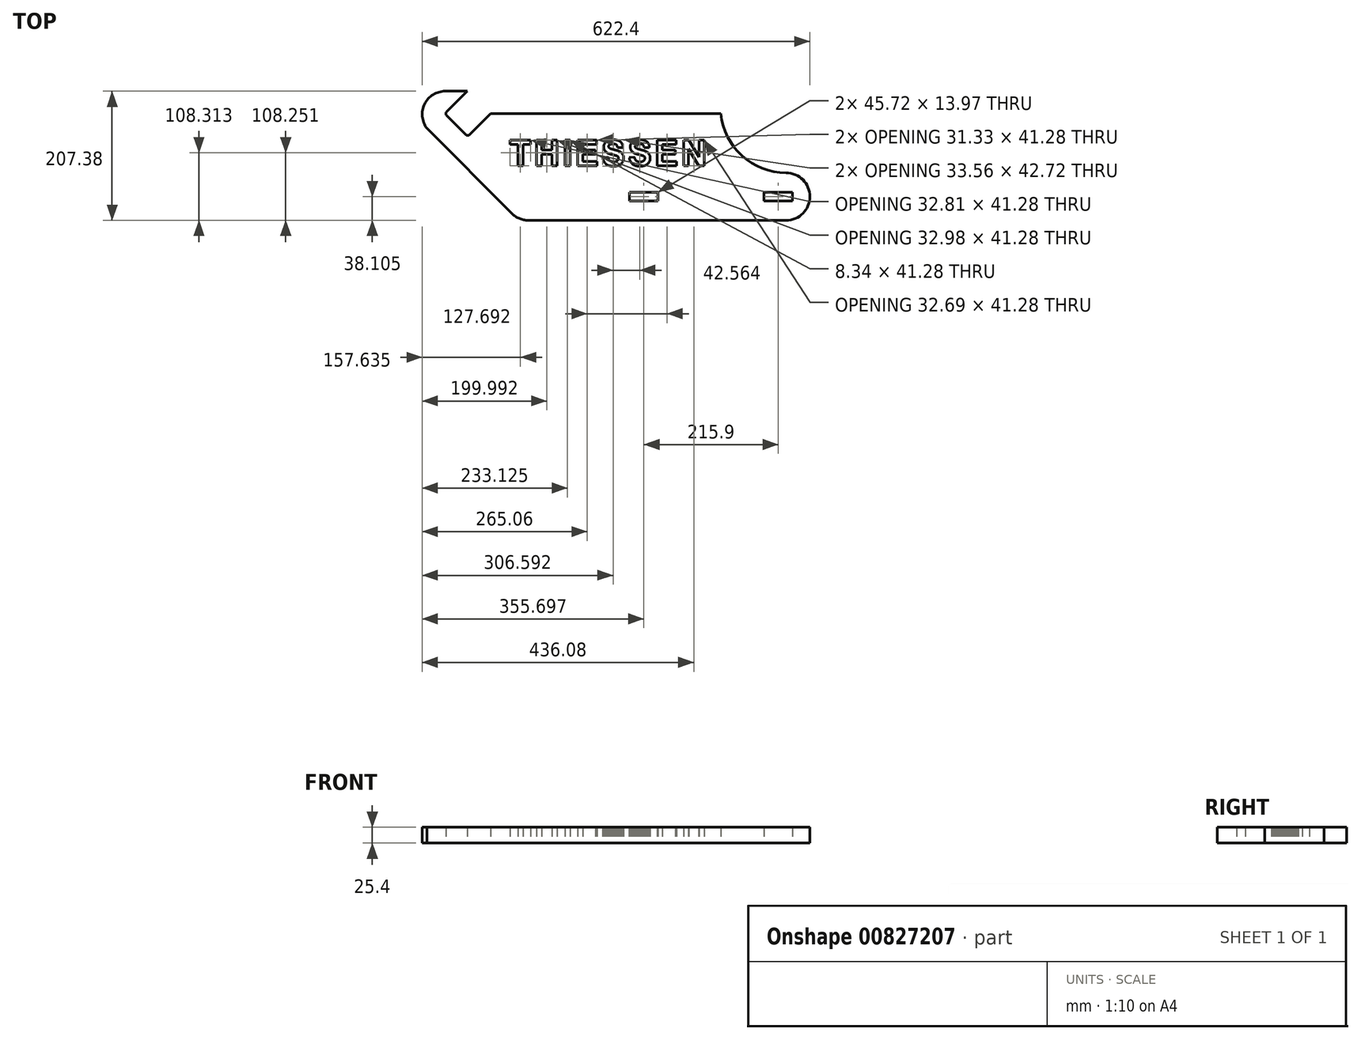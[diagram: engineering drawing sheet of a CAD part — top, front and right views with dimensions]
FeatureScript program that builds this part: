
annotation { "Feature Type Name" : "Feature", "Feature Type Description" : "" }
export const myFeature = defineFeature(function(context is Context, id is Id, definition is map)
    precondition{}
    {
        {
            var Q0;
            Q0=qCreatedBy(makeId("Top.planeOp"),FACE);
            var sketch = newSketch(context, id + "F0", { "sketchPlane" : qUnion([Q0])});
            skLineSegment(sketch, "E0", {"start": v(-238.98, 103.69) * mm, "end": v(-274, 103.69) * mm});
            skArc(sketch, "E1", {"start": v(-274, 103.69) * mm, "mid": v(-307.3, 83.06) * mm, "end": v(-303.67, 44.05) * mm});
            skArc(sketch, "E2", {"start": v(-167.33, -92.8) * mm, "mid": v(-155.26, -100.85) * mm, "end": v(-141.02, -103.69) * mm});
            skLineSegment(sketch, "E3", {"start": v(-141.02, -103.69) * mm, "end": v(273.1, -103.69) * mm});
            skArc(sketch, "E4", {"start": v(273.1, -103.69) * mm, "mid": v(311.2, -65.59) * mm, "end": v(273.1, -27.49) * mm});
            skArc(sketch, "E5", {"start": v(168.32, 67.76) * mm, "mid": v(202.3, -0.11) * mm, "end": v(273.1, -27.49) * mm});
            skLineSegment(sketch, "E6", {"start": v(-201.26, 67.76) * mm, "end": v(168.32, 67.76) * mm});
            skLineSegment(sketch, "E7", {"start": v(-303.67, 44.05) * mm, "end": v(-167.33, -92.8) * mm});
            skLineSegment(sketch, "E8", {"start": v(-272.2, 70.46) * mm, "end": v(-238.98, 103.69) * mm});
            skLineSegment(sketch, "E9", {"start": v(-240.77, 33.64) * mm, "end": v(-272.2, 65.07) * mm});
            skLineSegment(sketch, "E10", {"start": v(-201.26, 67.76) * mm, "end": v(-235.38, 33.64) * mm});
            skLineSegment(sketch, "E11", {"start": v(67.36, -58.6) * mm, "end": v(21.64, -58.6) * mm});
            skLineSegment(sketch, "E12", {"start": v(21.64, -72.57) * mm, "end": v(21.64, -58.6) * mm});
            skLineSegment(sketch, "E13", {"start": v(67.36, -72.57) * mm, "end": v(21.64, -72.57) * mm});
            skLineSegment(sketch, "E14", {"start": v(67.36, -72.57) * mm, "end": v(67.36, -58.6) * mm});
            skLineSegment(sketch, "E15", {"start": v(283.26, -58.6) * mm, "end": v(237.54, -58.6) * mm});
            skLineSegment(sketch, "E16", {"start": v(283.26, -72.57) * mm, "end": v(283.26, -58.6) * mm});
            skLineSegment(sketch, "E17", {"start": v(283.26, -72.57) * mm, "end": v(237.54, -72.57) * mm});
            skLineSegment(sketch, "E18", {"start": v(237.54, -72.57) * mm, "end": v(237.54, -58.6) * mm});
            skArc(sketch, "E19", {"start": v(-240.77, 33.64) * mm, "mid": v(-238.08, 32.52) * mm, "end": v(-235.38, 33.64) * mm});
            skArc(sketch, "E20", {"start": v(-272.2, 70.46) * mm, "mid": v(-273.32, 67.76) * mm, "end": v(-272.2, 65.07) * mm});
            skLineSegment(sketch, "E21", {"start": v(-157.71, -16.01) * mm, "end": v(-157.71, 18.28) * mm});
            skLineSegment(sketch, "E22", {"start": v(-157.71, 18.28) * mm, "end": v(-169.97, 18.28) * mm});
            skLineSegment(sketch, "E23", {"start": v(-169.97, 18.28) * mm, "end": v(-169.97, 25.26) * mm});
            skLineSegment(sketch, "E24", {"start": v(-169.97, 25.26) * mm, "end": v(-137.16, 25.26) * mm});
            skLineSegment(sketch, "E25", {"start": v(-137.16, 25.26) * mm, "end": v(-137.16, 18.28) * mm});
            skLineSegment(sketch, "E26", {"start": v(-137.16, 18.28) * mm, "end": v(-149.38, 18.28) * mm});
            skLineSegment(sketch, "E27", {"start": v(-149.38, 18.28) * mm, "end": v(-149.38, -16.01) * mm});
            skLineSegment(sketch, "E28", {"start": v(-149.38, -16.01) * mm, "end": v(-157.71, -16.01) * mm});
            skLineSegment(sketch, "E29", {"start": v(-127.7, -16.01) * mm, "end": v(-127.7, 25.26) * mm});
            skLineSegment(sketch, "E30", {"start": v(-127.7, 25.26) * mm, "end": v(-119.36, 25.26) * mm});
            skLineSegment(sketch, "E31", {"start": v(-119.36, 25.26) * mm, "end": v(-119.36, 9) * mm});
            skLineSegment(sketch, "E32", {"start": v(-119.36, 9) * mm, "end": v(-103.06, 9) * mm});
            skLineSegment(sketch, "E33", {"start": v(-103.06, 9) * mm, "end": v(-103.06, 25.26) * mm});
            skLineSegment(sketch, "E34", {"start": v(-103.06, 25.26) * mm, "end": v(-94.72, 25.26) * mm});
            skLineSegment(sketch, "E35", {"start": v(-94.72, 25.26) * mm, "end": v(-94.72, -16.01) * mm});
            skLineSegment(sketch, "E36", {"start": v(-94.72, -16.01) * mm, "end": v(-103.06, -16.01) * mm});
            skLineSegment(sketch, "E37", {"start": v(-103.06, -16.01) * mm, "end": v(-103.06, 2.02) * mm});
            skLineSegment(sketch, "E38", {"start": v(-103.06, 2.02) * mm, "end": v(-119.36, 2.02) * mm});
            skLineSegment(sketch, "E39", {"start": v(-119.36, 2.02) * mm, "end": v(-119.36, -16.01) * mm});
            skLineSegment(sketch, "E40", {"start": v(-119.36, -16.01) * mm, "end": v(-127.7, -16.01) * mm});
            skLineSegment(sketch, "E41", {"start": v(-82.24, -16.01) * mm, "end": v(-82.24, 25.26) * mm});
            skLineSegment(sketch, "E42", {"start": v(-82.24, 25.26) * mm, "end": v(-73.9, 25.26) * mm});
            skLineSegment(sketch, "E43", {"start": v(-73.9, 25.26) * mm, "end": v(-73.9, -16.01) * mm});
            skLineSegment(sketch, "E44", {"start": v(-73.9, -16.01) * mm, "end": v(-82.24, -16.01) * mm});
            skLineSegment(sketch, "E45", {"start": v(-61.8, -16.01) * mm, "end": v(-61.8, 25.26) * mm});
            skLineSegment(sketch, "E46", {"start": v(-61.8, 25.26) * mm, "end": v(-31.26, 25.26) * mm});
            skLineSegment(sketch, "E47", {"start": v(-31.26, 25.26) * mm, "end": v(-31.26, 18.28) * mm});
            skLineSegment(sketch, "E48", {"start": v(-31.26, 18.28) * mm, "end": v(-53.47, 18.28) * mm});
            skLineSegment(sketch, "E49", {"start": v(-53.47, 18.28) * mm, "end": v(-53.47, 9.12) * mm});
            skLineSegment(sketch, "E50", {"start": v(-53.47, 9.12) * mm, "end": v(-32.79, 9.12) * mm});
            skLineSegment(sketch, "E51", {"start": v(-32.79, 9.12) * mm, "end": v(-32.79, 2.15) * mm});
            skLineSegment(sketch, "E52", {"start": v(-32.79, 2.15) * mm, "end": v(-53.47, 2.15) * mm});
            skLineSegment(sketch, "E53", {"start": v(-53.47, 2.15) * mm, "end": v(-53.47, -9.04) * mm});
            skLineSegment(sketch, "E54", {"start": v(-53.47, -9.04) * mm, "end": v(-30.48, -9.04) * mm});
            skLineSegment(sketch, "E55", {"start": v(-30.48, -9.04) * mm, "end": v(-30.48, -16.01) * mm});
            skLineSegment(sketch, "E56", {"start": v(-30.48, -16.01) * mm, "end": v(-61.8, -16.01) * mm});
            skLineSegment(sketch, "E57", {"start": v(-21.39, -2.64) * mm, "end": v(-13.3, -1.86) * mm});
            skLineSegment(sketch, "E58", {"start": v(-13.3, -1.86) * mm, "end": v(-13.09, -2.85) * mm});
            skLineSegment(sketch, "E59", {"start": v(-13.09, -2.85) * mm, "end": v(-12.84, -3.77) * mm});
            skLineSegment(sketch, "E60", {"start": v(-12.84, -3.77) * mm, "end": v(-12.53, -4.62) * mm});
            skLineSegment(sketch, "E61", {"start": v(-12.53, -4.62) * mm, "end": v(-12.19, -5.4) * mm});
            skLineSegment(sketch, "E62", {"start": v(-12.19, -5.4) * mm, "end": v(-11.8, -6.12) * mm});
            skLineSegment(sketch, "E63", {"start": v(-11.8, -6.12) * mm, "end": v(-11.35, -6.77) * mm});
            skLineSegment(sketch, "E64", {"start": v(-11.35, -6.77) * mm, "end": v(-10.86, -7.35) * mm});
            skLineSegment(sketch, "E65", {"start": v(-10.86, -7.35) * mm, "end": v(-10.32, -7.86) * mm});
            skLineSegment(sketch, "E66", {"start": v(-10.32, -7.86) * mm, "end": v(-9.74, -8.31) * mm});
            skLineSegment(sketch, "E67", {"start": v(-9.74, -8.31) * mm, "end": v(-9.1, -8.7) * mm});
            skLineSegment(sketch, "E68", {"start": v(-9.1, -8.7) * mm, "end": v(-8.42, -9.03) * mm});
            skLineSegment(sketch, "E69", {"start": v(-8.42, -9.03) * mm, "end": v(-7.7, -9.3) * mm});
            skLineSegment(sketch, "E70", {"start": v(-7.7, -9.3) * mm, "end": v(-6.91, -9.51) * mm});
            skLineSegment(sketch, "E71", {"start": v(-6.91, -9.51) * mm, "end": v(-6.08, -9.66) * mm});
            skLineSegment(sketch, "E72", {"start": v(-6.08, -9.66) * mm, "end": v(-5.2, -9.75) * mm});
            skLineSegment(sketch, "E73", {"start": v(-5.2, -9.75) * mm, "end": v(-4.28, -9.78) * mm});
            skLineSegment(sketch, "E74", {"start": v(-4.28, -9.78) * mm, "end": v(-3.3, -9.76) * mm});
            skLineSegment(sketch, "E75", {"start": v(-3.3, -9.76) * mm, "end": v(-2.4, -9.68) * mm});
            skLineSegment(sketch, "E76", {"start": v(-2.4, -9.68) * mm, "end": v(-1.54, -9.54) * mm});
            skLineSegment(sketch, "E77", {"start": v(-1.54, -9.54) * mm, "end": v(-0.75, -9.36) * mm});
            skLineSegment(sketch, "E78", {"start": v(-0.75, -9.36) * mm, "end": v(-0.02, -9.12) * mm});
            skLineSegment(sketch, "E79", {"start": v(-0.02, -9.12) * mm, "end": v(0.65, -8.82) * mm});
            skLineSegment(sketch, "E80", {"start": v(0.65, -8.82) * mm, "end": v(1.25, -8.48) * mm});
            skLineSegment(sketch, "E81", {"start": v(1.25, -8.48) * mm, "end": v(1.8, -8.08) * mm});
            skLineSegment(sketch, "E82", {"start": v(1.8, -8.08) * mm, "end": v(2.41, -7.5) * mm});
            skLineSegment(sketch, "E83", {"start": v(2.41, -7.5) * mm, "end": v(2.93, -6.88) * mm});
            skLineSegment(sketch, "E84", {"start": v(2.93, -6.88) * mm, "end": v(3.32, -6.23) * mm});
            skLineSegment(sketch, "E85", {"start": v(3.32, -6.23) * mm, "end": v(3.6, -5.55) * mm});
            skLineSegment(sketch, "E86", {"start": v(3.6, -5.55) * mm, "end": v(3.78, -4.83) * mm});
            skLineSegment(sketch, "E87", {"start": v(3.78, -4.83) * mm, "end": v(3.83, -4.09) * mm});
            skLineSegment(sketch, "E88", {"start": v(3.83, -4.09) * mm, "end": v(3.74, -3.16) * mm});
            skLineSegment(sketch, "E89", {"start": v(3.74, -3.16) * mm, "end": v(3.45, -2.33) * mm});
            skLineSegment(sketch, "E90", {"start": v(3.45, -2.33) * mm, "end": v(2.97, -1.6) * mm});
            skLineSegment(sketch, "E91", {"start": v(2.97, -1.6) * mm, "end": v(2.47, -1.1) * mm});
            skLineSegment(sketch, "E92", {"start": v(2.47, -1.1) * mm, "end": v(1.8, -0.63) * mm});
            skLineSegment(sketch, "E93", {"start": v(1.8, -0.63) * mm, "end": v(0.97, -0.2) * mm});
            skLineSegment(sketch, "E94", {"start": v(0.97, -0.2) * mm, "end": v(-0.02, 0.2) * mm});
            skLineSegment(sketch, "E95", {"start": v(-0.02, 0.2) * mm, "end": v(-0.45, 0.34) * mm});
            skLineSegment(sketch, "E96", {"start": v(-0.45, 0.34) * mm, "end": v(-1, 0.5) * mm});
            skLineSegment(sketch, "E97", {"start": v(-1, 0.5) * mm, "end": v(-1.65, 0.69) * mm});
            skLineSegment(sketch, "E98", {"start": v(-1.65, 0.69) * mm, "end": v(-2.42, 0.9) * mm});
            skLineSegment(sketch, "E99", {"start": v(-2.42, 0.9) * mm, "end": v(-3.32, 1.14) * mm});
            skLineSegment(sketch, "E100", {"start": v(-3.32, 1.14) * mm, "end": v(-4.33, 1.4) * mm});
            skLineSegment(sketch, "E101", {"start": v(-4.33, 1.4) * mm, "end": v(-5.45, 1.69) * mm});
            skLineSegment(sketch, "E102", {"start": v(-5.45, 1.69) * mm, "end": v(-6.7, 2) * mm});
            skLineSegment(sketch, "E103", {"start": v(-6.7, 2) * mm, "end": v(-7.78, 2.28) * mm});
            skLineSegment(sketch, "E104", {"start": v(-7.78, 2.28) * mm, "end": v(-8.82, 2.58) * mm});
            skLineSegment(sketch, "E105", {"start": v(-8.82, 2.58) * mm, "end": v(-9.8, 2.88) * mm});
            skLineSegment(sketch, "E106", {"start": v(-9.8, 2.88) * mm, "end": v(-10.72, 3.2) * mm});
            skLineSegment(sketch, "E107", {"start": v(-10.72, 3.2) * mm, "end": v(-11.59, 3.52) * mm});
            skLineSegment(sketch, "E108", {"start": v(-11.59, 3.52) * mm, "end": v(-12.4, 3.85) * mm});
            skLineSegment(sketch, "E109", {"start": v(-12.4, 3.85) * mm, "end": v(-13.15, 4.2) * mm});
            skLineSegment(sketch, "E110", {"start": v(-13.15, 4.2) * mm, "end": v(-13.85, 4.56) * mm});
            skLineSegment(sketch, "E111", {"start": v(-13.85, 4.56) * mm, "end": v(-14.5, 4.92) * mm});
            skLineSegment(sketch, "E112", {"start": v(-14.5, 4.92) * mm, "end": v(-15.09, 5.3) * mm});
            skLineSegment(sketch, "E113", {"start": v(-15.09, 5.3) * mm, "end": v(-15.62, 5.69) * mm});
            skLineSegment(sketch, "E114", {"start": v(-15.62, 5.69) * mm, "end": v(-16.1, 6.09) * mm});
            skLineSegment(sketch, "E115", {"start": v(-16.1, 6.09) * mm, "end": v(-16.76, 6.72) * mm});
            skLineSegment(sketch, "E116", {"start": v(-16.76, 6.72) * mm, "end": v(-17.36, 7.38) * mm});
            skLineSegment(sketch, "E117", {"start": v(-17.36, 7.38) * mm, "end": v(-17.89, 8.06) * mm});
            skLineSegment(sketch, "E118", {"start": v(-17.89, 8.06) * mm, "end": v(-18.36, 8.76) * mm});
            skLineSegment(sketch, "E119", {"start": v(-18.36, 8.76) * mm, "end": v(-18.77, 9.5) * mm});
            skLineSegment(sketch, "E120", {"start": v(-18.77, 9.5) * mm, "end": v(-19.11, 10.25) * mm});
            skLineSegment(sketch, "E121", {"start": v(-19.11, 10.25) * mm, "end": v(-19.4, 11.03) * mm});
            skLineSegment(sketch, "E122", {"start": v(-19.4, 11.03) * mm, "end": v(-19.62, 11.83) * mm});
            skLineSegment(sketch, "E123", {"start": v(-19.62, 11.83) * mm, "end": v(-19.77, 12.66) * mm});
            skLineSegment(sketch, "E124", {"start": v(-19.77, 12.66) * mm, "end": v(-19.87, 13.52) * mm});
            skLineSegment(sketch, "E125", {"start": v(-19.87, 13.52) * mm, "end": v(-19.9, 14.4) * mm});
            skLineSegment(sketch, "E126", {"start": v(-19.9, 14.4) * mm, "end": v(-19.86, 15.3) * mm});
            skLineSegment(sketch, "E127", {"start": v(-19.86, 15.3) * mm, "end": v(-19.75, 16.17) * mm});
            skLineSegment(sketch, "E128", {"start": v(-19.75, 16.17) * mm, "end": v(-19.57, 17.03) * mm});
            skLineSegment(sketch, "E129", {"start": v(-19.57, 17.03) * mm, "end": v(-19.32, 17.87) * mm});
            skLineSegment(sketch, "E130", {"start": v(-19.32, 17.87) * mm, "end": v(-18.99, 18.7) * mm});
            skLineSegment(sketch, "E131", {"start": v(-18.99, 18.7) * mm, "end": v(-18.59, 19.5) * mm});
            skLineSegment(sketch, "E132", {"start": v(-18.59, 19.5) * mm, "end": v(-18.11, 20.3) * mm});
            skLineSegment(sketch, "E133", {"start": v(-18.11, 20.3) * mm, "end": v(-17.64, 20.97) * mm});
            skLineSegment(sketch, "E134", {"start": v(-17.64, 20.97) * mm, "end": v(-17.12, 21.6) * mm});
            skLineSegment(sketch, "E135", {"start": v(-17.12, 21.6) * mm, "end": v(-16.55, 22.18) * mm});
            skLineSegment(sketch, "E136", {"start": v(-16.55, 22.18) * mm, "end": v(-15.93, 22.72) * mm});
            skLineSegment(sketch, "E137", {"start": v(-15.93, 22.72) * mm, "end": v(-15.26, 23.22) * mm});
            skLineSegment(sketch, "E138", {"start": v(-15.26, 23.22) * mm, "end": v(-14.55, 23.68) * mm});
            skLineSegment(sketch, "E139", {"start": v(-14.55, 23.68) * mm, "end": v(-13.78, 24.1) * mm});
            skLineSegment(sketch, "E140", {"start": v(-13.78, 24.1) * mm, "end": v(-12.96, 24.48) * mm});
            skLineSegment(sketch, "E141", {"start": v(-12.96, 24.48) * mm, "end": v(-12.2, 24.79) * mm});
            skLineSegment(sketch, "E142", {"start": v(-12.2, 24.79) * mm, "end": v(-11.4, 25.05) * mm});
            skLineSegment(sketch, "E143", {"start": v(-11.4, 25.05) * mm, "end": v(-10.57, 25.28) * mm});
            skLineSegment(sketch, "E144", {"start": v(-10.57, 25.28) * mm, "end": v(-9.7, 25.48) * mm});
            skLineSegment(sketch, "E145", {"start": v(-9.7, 25.48) * mm, "end": v(-8.8, 25.64) * mm});
            skLineSegment(sketch, "E146", {"start": v(-8.8, 25.64) * mm, "end": v(-7.86, 25.76) * mm});
            skLineSegment(sketch, "E147", {"start": v(-7.86, 25.76) * mm, "end": v(-6.89, 25.85) * mm});
            skLineSegment(sketch, "E148", {"start": v(-6.89, 25.85) * mm, "end": v(-5.88, 25.9) * mm});
            skLineSegment(sketch, "E149", {"start": v(-5.88, 25.9) * mm, "end": v(-4.84, 25.92) * mm});
            skLineSegment(sketch, "E150", {"start": v(-4.84, 25.92) * mm, "end": v(-3.75, 25.9) * mm});
            skLineSegment(sketch, "E151", {"start": v(-3.75, 25.9) * mm, "end": v(-2.7, 25.85) * mm});
            skLineSegment(sketch, "E152", {"start": v(-2.7, 25.85) * mm, "end": v(-1.7, 25.76) * mm});
            skLineSegment(sketch, "E153", {"start": v(-1.7, 25.76) * mm, "end": v(-0.72, 25.64) * mm});
            skLineSegment(sketch, "E154", {"start": v(-0.72, 25.64) * mm, "end": v(0.22, 25.49) * mm});
            skLineSegment(sketch, "E155", {"start": v(0.22, 25.49) * mm, "end": v(1.1, 25.3) * mm});
            skLineSegment(sketch, "E156", {"start": v(1.1, 25.3) * mm, "end": v(1.96, 25.07) * mm});
            skLineSegment(sketch, "E157", {"start": v(1.96, 25.07) * mm, "end": v(2.78, 24.8) * mm});
            skLineSegment(sketch, "E158", {"start": v(2.78, 24.8) * mm, "end": v(3.56, 24.51) * mm});
            skLineSegment(sketch, "E159", {"start": v(3.56, 24.51) * mm, "end": v(4.3, 24.18) * mm});
            skLineSegment(sketch, "E160", {"start": v(4.3, 24.18) * mm, "end": v(5, 23.82) * mm});
            skLineSegment(sketch, "E161", {"start": v(5, 23.82) * mm, "end": v(5.65, 23.42) * mm});
            skLineSegment(sketch, "E162", {"start": v(5.65, 23.42) * mm, "end": v(6.27, 22.98) * mm});
            skLineSegment(sketch, "E163", {"start": v(6.27, 22.98) * mm, "end": v(6.85, 22.51) * mm});
            skLineSegment(sketch, "E164", {"start": v(6.85, 22.51) * mm, "end": v(7.48, 21.93) * mm});
            skLineSegment(sketch, "E165", {"start": v(7.48, 21.93) * mm, "end": v(8.06, 21.31) * mm});
            skLineSegment(sketch, "E166", {"start": v(8.06, 21.31) * mm, "end": v(8.58, 20.67) * mm});
            skLineSegment(sketch, "E167", {"start": v(8.58, 20.67) * mm, "end": v(9.05, 19.99) * mm});
            skLineSegment(sketch, "E168", {"start": v(9.05, 19.99) * mm, "end": v(9.48, 19.28) * mm});
            skLineSegment(sketch, "E169", {"start": v(9.48, 19.28) * mm, "end": v(9.84, 18.53) * mm});
            skLineSegment(sketch, "E170", {"start": v(9.84, 18.53) * mm, "end": v(10.16, 17.76) * mm});
            skLineSegment(sketch, "E171", {"start": v(10.16, 17.76) * mm, "end": v(10.43, 16.95) * mm});
            skLineSegment(sketch, "E172", {"start": v(10.43, 16.95) * mm, "end": v(10.64, 16.12) * mm});
            skLineSegment(sketch, "E173", {"start": v(10.64, 16.12) * mm, "end": v(10.8, 15.25) * mm});
            skLineSegment(sketch, "E174", {"start": v(10.8, 15.25) * mm, "end": v(10.92, 14.35) * mm});
            skLineSegment(sketch, "E175", {"start": v(10.92, 14.35) * mm, "end": v(10.97, 13.41) * mm});
            skLineSegment(sketch, "E176", {"start": v(10.97, 13.41) * mm, "end": v(2.64, 13.04) * mm});
            skLineSegment(sketch, "E177", {"start": v(2.64, 13.04) * mm, "end": v(2.42, 14.06) * mm});
            skLineSegment(sketch, "E178", {"start": v(2.42, 14.06) * mm, "end": v(2.14, 14.97) * mm});
            skLineSegment(sketch, "E179", {"start": v(2.14, 14.97) * mm, "end": v(1.8, 15.78) * mm});
            skLineSegment(sketch, "E180", {"start": v(1.8, 15.78) * mm, "end": v(1.38, 16.5) * mm});
            skLineSegment(sketch, "E181", {"start": v(1.38, 16.5) * mm, "end": v(0.9, 17.11) * mm});
            skLineSegment(sketch, "E182", {"start": v(0.9, 17.11) * mm, "end": v(0.34, 17.63) * mm});
            skLineSegment(sketch, "E183", {"start": v(0.34, 17.63) * mm, "end": v(-0.2, 18) * mm});
            skLineSegment(sketch, "E184", {"start": v(-0.2, 18) * mm, "end": v(-0.8, 18.31) * mm});
            skLineSegment(sketch, "E185", {"start": v(-0.8, 18.31) * mm, "end": v(-1.49, 18.57) * mm});
            skLineSegment(sketch, "E186", {"start": v(-1.49, 18.57) * mm, "end": v(-2.24, 18.77) * mm});
            skLineSegment(sketch, "E187", {"start": v(-2.24, 18.77) * mm, "end": v(-3.06, 18.91) * mm});
            skLineSegment(sketch, "E188", {"start": v(-3.06, 18.91) * mm, "end": v(-3.96, 19) * mm});
            skLineSegment(sketch, "E189", {"start": v(-3.96, 19) * mm, "end": v(-4.93, 19.03) * mm});
            skLineSegment(sketch, "E190", {"start": v(-4.93, 19.03) * mm, "end": v(-5.93, 19) * mm});
            skLineSegment(sketch, "E191", {"start": v(-5.93, 19) * mm, "end": v(-6.87, 18.9) * mm});
            skLineSegment(sketch, "E192", {"start": v(-6.87, 18.9) * mm, "end": v(-7.75, 18.75) * mm});
            skLineSegment(sketch, "E193", {"start": v(-7.75, 18.75) * mm, "end": v(-8.56, 18.54) * mm});
            skLineSegment(sketch, "E194", {"start": v(-8.56, 18.54) * mm, "end": v(-9.3, 18.26) * mm});
            skLineSegment(sketch, "E195", {"start": v(-9.3, 18.26) * mm, "end": v(-10, 17.93) * mm});
            skLineSegment(sketch, "E196", {"start": v(-10, 17.93) * mm, "end": v(-10.61, 17.53) * mm});
            skLineSegment(sketch, "E197", {"start": v(-10.61, 17.53) * mm, "end": v(-11.2, 17.01) * mm});
            skLineSegment(sketch, "E198", {"start": v(-11.2, 17.01) * mm, "end": v(-11.6, 16.41) * mm});
            skLineSegment(sketch, "E199", {"start": v(-11.6, 16.41) * mm, "end": v(-11.85, 15.73) * mm});
            skLineSegment(sketch, "E200", {"start": v(-11.85, 15.73) * mm, "end": v(-11.93, 14.96) * mm});
            skLineSegment(sketch, "E201", {"start": v(-11.93, 14.96) * mm, "end": v(-11.86, 14.26) * mm});
            skLineSegment(sketch, "E202", {"start": v(-11.86, 14.26) * mm, "end": v(-11.62, 13.6) * mm});
            skLineSegment(sketch, "E203", {"start": v(-11.62, 13.6) * mm, "end": v(-11.24, 13) * mm});
            skLineSegment(sketch, "E204", {"start": v(-11.24, 13) * mm, "end": v(-10.7, 12.45) * mm});
            skLineSegment(sketch, "E205", {"start": v(-10.7, 12.45) * mm, "end": v(-10.33, 12.19) * mm});
            skLineSegment(sketch, "E206", {"start": v(-10.33, 12.19) * mm, "end": v(-9.88, 11.92) * mm});
            skLineSegment(sketch, "E207", {"start": v(-9.88, 11.92) * mm, "end": v(-9.34, 11.65) * mm});
            skLineSegment(sketch, "E208", {"start": v(-9.34, 11.65) * mm, "end": v(-8.71, 11.37) * mm});
            skLineSegment(sketch, "E209", {"start": v(-8.71, 11.37) * mm, "end": v(-8, 11.1) * mm});
            skLineSegment(sketch, "E210", {"start": v(-8, 11.1) * mm, "end": v(-7.18, 10.82) * mm});
            skLineSegment(sketch, "E211", {"start": v(-7.18, 10.82) * mm, "end": v(-6.28, 10.54) * mm});
            skLineSegment(sketch, "E212", {"start": v(-6.28, 10.54) * mm, "end": v(-5.29, 10.26) * mm});
            skLineSegment(sketch, "E213", {"start": v(-5.29, 10.26) * mm, "end": v(-4.2, 9.98) * mm});
            skLineSegment(sketch, "E214", {"start": v(-4.2, 9.98) * mm, "end": v(-3.04, 9.7) * mm});
            skLineSegment(sketch, "E215", {"start": v(-3.04, 9.7) * mm, "end": v(-1.96, 9.43) * mm});
            skLineSegment(sketch, "E216", {"start": v(-1.96, 9.43) * mm, "end": v(-0.93, 9.17) * mm});
            skLineSegment(sketch, "E217", {"start": v(-0.93, 9.17) * mm, "end": v(0.05, 8.9) * mm});
            skLineSegment(sketch, "E218", {"start": v(0.05, 8.9) * mm, "end": v(0.97, 8.63) * mm});
            skLineSegment(sketch, "E219", {"start": v(0.97, 8.63) * mm, "end": v(1.84, 8.36) * mm});
            skLineSegment(sketch, "E220", {"start": v(1.84, 8.36) * mm, "end": v(2.66, 8.1) * mm});
            skLineSegment(sketch, "E221", {"start": v(2.66, 8.1) * mm, "end": v(3.42, 7.82) * mm});
            skLineSegment(sketch, "E222", {"start": v(3.42, 7.82) * mm, "end": v(4.14, 7.55) * mm});
            skLineSegment(sketch, "E223", {"start": v(4.14, 7.55) * mm, "end": v(4.8, 7.27) * mm});
            skLineSegment(sketch, "E224", {"start": v(4.8, 7.27) * mm, "end": v(5.4, 7) * mm});
            skLineSegment(sketch, "E225", {"start": v(5.4, 7) * mm, "end": v(5.96, 6.72) * mm});
            skLineSegment(sketch, "E226", {"start": v(5.96, 6.72) * mm, "end": v(6.77, 6.26) * mm});
            skLineSegment(sketch, "E227", {"start": v(6.77, 6.26) * mm, "end": v(7.52, 5.75) * mm});
            skLineSegment(sketch, "E228", {"start": v(7.52, 5.75) * mm, "end": v(8.23, 5.2) * mm});
            skLineSegment(sketch, "E229", {"start": v(8.23, 5.2) * mm, "end": v(8.88, 4.6) * mm});
            skLineSegment(sketch, "E230", {"start": v(8.88, 4.6) * mm, "end": v(9.48, 3.95) * mm});
            skLineSegment(sketch, "E231", {"start": v(9.48, 3.95) * mm, "end": v(10.03, 3.26) * mm});
            skLineSegment(sketch, "E232", {"start": v(10.03, 3.26) * mm, "end": v(10.52, 2.53) * mm});
            skLineSegment(sketch, "E233", {"start": v(10.52, 2.53) * mm, "end": v(10.9, 1.84) * mm});
            skLineSegment(sketch, "E234", {"start": v(10.9, 1.84) * mm, "end": v(11.24, 1.12) * mm});
            skLineSegment(sketch, "E235", {"start": v(11.24, 1.12) * mm, "end": v(11.53, 0.35) * mm});
            skLineSegment(sketch, "E236", {"start": v(11.53, 0.35) * mm, "end": v(11.76, -0.45) * mm});
            skLineSegment(sketch, "E237", {"start": v(11.76, -0.45) * mm, "end": v(11.94, -1.29) * mm});
            skLineSegment(sketch, "E238", {"start": v(11.94, -1.29) * mm, "end": v(12.07, -2.17) * mm});
            skLineSegment(sketch, "E239", {"start": v(12.07, -2.17) * mm, "end": v(12.15, -3.09) * mm});
            skLineSegment(sketch, "E240", {"start": v(12.15, -3.09) * mm, "end": v(12.17, -4.05) * mm});
            skLineSegment(sketch, "E241", {"start": v(12.17, -4.05) * mm, "end": v(12.14, -4.93) * mm});
            skLineSegment(sketch, "E242", {"start": v(12.14, -4.93) * mm, "end": v(12.05, -5.8) * mm});
            skLineSegment(sketch, "E243", {"start": v(12.05, -5.8) * mm, "end": v(11.9, -6.64) * mm});
            skLineSegment(sketch, "E244", {"start": v(11.9, -6.64) * mm, "end": v(11.68, -7.48) * mm});
            skLineSegment(sketch, "E245", {"start": v(11.68, -7.48) * mm, "end": v(11.4, -8.3) * mm});
            skLineSegment(sketch, "E246", {"start": v(11.4, -8.3) * mm, "end": v(11.06, -9.11) * mm});
            skLineSegment(sketch, "E247", {"start": v(11.06, -9.11) * mm, "end": v(10.66, -9.9) * mm});
            skLineSegment(sketch, "E248", {"start": v(10.66, -9.9) * mm, "end": v(10.2, -10.7) * mm});
            skLineSegment(sketch, "E249", {"start": v(10.2, -10.7) * mm, "end": v(9.68, -11.44) * mm});
            skLineSegment(sketch, "E250", {"start": v(9.68, -11.44) * mm, "end": v(9.11, -12.14) * mm});
            skLineSegment(sketch, "E251", {"start": v(9.11, -12.14) * mm, "end": v(8.5, -12.79) * mm});
            skLineSegment(sketch, "E252", {"start": v(8.5, -12.79) * mm, "end": v(7.82, -13.39) * mm});
            skLineSegment(sketch, "E253", {"start": v(7.82, -13.39) * mm, "end": v(7.1, -13.94) * mm});
            skLineSegment(sketch, "E254", {"start": v(7.1, -13.94) * mm, "end": v(6.33, -14.44) * mm});
            skLineSegment(sketch, "E255", {"start": v(6.33, -14.44) * mm, "end": v(5.5, -14.9) * mm});
            skLineSegment(sketch, "E256", {"start": v(5.5, -14.9) * mm, "end": v(4.63, -15.3) * mm});
            skLineSegment(sketch, "E257", {"start": v(4.63, -15.3) * mm, "end": v(3.89, -15.58) * mm});
            skLineSegment(sketch, "E258", {"start": v(3.89, -15.58) * mm, "end": v(3.11, -15.84) * mm});
            skLineSegment(sketch, "E259", {"start": v(3.11, -15.84) * mm, "end": v(2.3, -16.06) * mm});
            skLineSegment(sketch, "E260", {"start": v(2.3, -16.06) * mm, "end": v(1.46, -16.26) * mm});
            skLineSegment(sketch, "E261", {"start": v(1.46, -16.26) * mm, "end": v(0.58, -16.42) * mm});
            skLineSegment(sketch, "E262", {"start": v(0.58, -16.42) * mm, "end": v(-0.34, -16.56) * mm});
            skLineSegment(sketch, "E263", {"start": v(-0.34, -16.56) * mm, "end": v(-1.29, -16.66) * mm});
            skLineSegment(sketch, "E264", {"start": v(-1.29, -16.66) * mm, "end": v(-2.27, -16.74) * mm});
            skLineSegment(sketch, "E265", {"start": v(-2.27, -16.74) * mm, "end": v(-3.3, -16.78) * mm});
            skLineSegment(sketch, "E266", {"start": v(-3.3, -16.78) * mm, "end": v(-4.35, -16.8) * mm});
            skLineSegment(sketch, "E267", {"start": v(-4.35, -16.8) * mm, "end": v(-5.45, -16.78) * mm});
            skLineSegment(sketch, "E268", {"start": v(-5.45, -16.78) * mm, "end": v(-6.52, -16.73) * mm});
            skLineSegment(sketch, "E269", {"start": v(-6.52, -16.73) * mm, "end": v(-7.54, -16.63) * mm});
            skLineSegment(sketch, "E270", {"start": v(-7.54, -16.63) * mm, "end": v(-8.53, -16.5) * mm});
            skLineSegment(sketch, "E271", {"start": v(-8.53, -16.5) * mm, "end": v(-9.48, -16.34) * mm});
            skLineSegment(sketch, "E272", {"start": v(-9.48, -16.34) * mm, "end": v(-10.4, -16.13) * mm});
            skLineSegment(sketch, "E273", {"start": v(-10.4, -16.13) * mm, "end": v(-11.27, -15.9) * mm});
            skLineSegment(sketch, "E274", {"start": v(-11.27, -15.9) * mm, "end": v(-12.11, -15.62) * mm});
            skLineSegment(sketch, "E275", {"start": v(-12.11, -15.62) * mm, "end": v(-12.92, -15.3) * mm});
            skLineSegment(sketch, "E276", {"start": v(-12.92, -15.3) * mm, "end": v(-13.68, -14.95) * mm});
            skLineSegment(sketch, "E277", {"start": v(-13.68, -14.95) * mm, "end": v(-14.41, -14.57) * mm});
            skLineSegment(sketch, "E278", {"start": v(-14.41, -14.57) * mm, "end": v(-15.1, -14.14) * mm});
            skLineSegment(sketch, "E279", {"start": v(-15.1, -14.14) * mm, "end": v(-15.76, -13.68) * mm});
            skLineSegment(sketch, "E280", {"start": v(-15.76, -13.68) * mm, "end": v(-16.37, -13.18) * mm});
            skLineSegment(sketch, "E281", {"start": v(-16.37, -13.18) * mm, "end": v(-17, -12.6) * mm});
            skLineSegment(sketch, "E282", {"start": v(-17, -12.6) * mm, "end": v(-17.59, -12) * mm});
            skLineSegment(sketch, "E283", {"start": v(-17.59, -12) * mm, "end": v(-18.13, -11.34) * mm});
            skLineSegment(sketch, "E284", {"start": v(-18.13, -11.34) * mm, "end": v(-18.64, -10.64) * mm});
            skLineSegment(sketch, "E285", {"start": v(-18.64, -10.64) * mm, "end": v(-19.1, -9.91) * mm});
            skLineSegment(sketch, "E286", {"start": v(-19.1, -9.91) * mm, "end": v(-19.53, -9.14) * mm});
            skLineSegment(sketch, "E287", {"start": v(-19.53, -9.14) * mm, "end": v(-19.91, -8.33) * mm});
            skLineSegment(sketch, "E288", {"start": v(-19.91, -8.33) * mm, "end": v(-20.26, -7.48) * mm});
            skLineSegment(sketch, "E289", {"start": v(-20.26, -7.48) * mm, "end": v(-20.56, -6.59) * mm});
            skLineSegment(sketch, "E290", {"start": v(-20.56, -6.59) * mm, "end": v(-20.83, -5.66) * mm});
            skLineSegment(sketch, "E291", {"start": v(-20.83, -5.66) * mm, "end": v(-21.05, -4.7) * mm});
            skLineSegment(sketch, "E292", {"start": v(-21.05, -4.7) * mm, "end": v(-21.24, -3.69) * mm});
            skLineSegment(sketch, "E293", {"start": v(-21.24, -3.69) * mm, "end": v(-21.39, -2.64) * mm});
            skLineSegment(sketch, "E294", {"start": v(21.18, -2.64) * mm, "end": v(29.27, -1.86) * mm});
            skLineSegment(sketch, "E295", {"start": v(29.27, -1.86) * mm, "end": v(29.47, -2.85) * mm});
            skLineSegment(sketch, "E296", {"start": v(29.47, -2.85) * mm, "end": v(29.73, -3.77) * mm});
            skLineSegment(sketch, "E297", {"start": v(29.73, -3.77) * mm, "end": v(30.03, -4.62) * mm});
            skLineSegment(sketch, "E298", {"start": v(30.03, -4.62) * mm, "end": v(30.38, -5.4) * mm});
            skLineSegment(sketch, "E299", {"start": v(30.38, -5.4) * mm, "end": v(30.77, -6.12) * mm});
            skLineSegment(sketch, "E300", {"start": v(30.77, -6.12) * mm, "end": v(31.21, -6.77) * mm});
            skLineSegment(sketch, "E301", {"start": v(31.21, -6.77) * mm, "end": v(31.7, -7.35) * mm});
            skLineSegment(sketch, "E302", {"start": v(31.7, -7.35) * mm, "end": v(32.24, -7.86) * mm});
            skLineSegment(sketch, "E303", {"start": v(32.24, -7.86) * mm, "end": v(32.82, -8.31) * mm});
            skLineSegment(sketch, "E304", {"start": v(32.82, -8.31) * mm, "end": v(33.46, -8.7) * mm});
            skLineSegment(sketch, "E305", {"start": v(33.46, -8.7) * mm, "end": v(34.14, -9.03) * mm});
            skLineSegment(sketch, "E306", {"start": v(34.14, -9.03) * mm, "end": v(34.87, -9.3) * mm});
            skLineSegment(sketch, "E307", {"start": v(34.87, -9.3) * mm, "end": v(35.65, -9.51) * mm});
            skLineSegment(sketch, "E308", {"start": v(35.65, -9.51) * mm, "end": v(36.48, -9.66) * mm});
            skLineSegment(sketch, "E309", {"start": v(36.48, -9.66) * mm, "end": v(37.36, -9.75) * mm});
            skLineSegment(sketch, "E310", {"start": v(37.36, -9.75) * mm, "end": v(38.28, -9.78) * mm});
            skLineSegment(sketch, "E311", {"start": v(38.28, -9.78) * mm, "end": v(39.26, -9.76) * mm});
            skLineSegment(sketch, "E312", {"start": v(39.26, -9.76) * mm, "end": v(40.17, -9.68) * mm});
            skLineSegment(sketch, "E313", {"start": v(40.17, -9.68) * mm, "end": v(41.03, -9.54) * mm});
            skLineSegment(sketch, "E314", {"start": v(41.03, -9.54) * mm, "end": v(41.82, -9.36) * mm});
            skLineSegment(sketch, "E315", {"start": v(41.82, -9.36) * mm, "end": v(42.54, -9.12) * mm});
            skLineSegment(sketch, "E316", {"start": v(42.54, -9.12) * mm, "end": v(43.2, -8.82) * mm});
            skLineSegment(sketch, "E317", {"start": v(43.2, -8.82) * mm, "end": v(43.81, -8.48) * mm});
            skLineSegment(sketch, "E318", {"start": v(43.81, -8.48) * mm, "end": v(44.35, -8.08) * mm});
            skLineSegment(sketch, "E319", {"start": v(44.35, -8.08) * mm, "end": v(44.98, -7.5) * mm});
            skLineSegment(sketch, "E320", {"start": v(44.98, -7.5) * mm, "end": v(45.49, -6.88) * mm});
            skLineSegment(sketch, "E321", {"start": v(45.49, -6.88) * mm, "end": v(45.89, -6.23) * mm});
            skLineSegment(sketch, "E322", {"start": v(45.89, -6.23) * mm, "end": v(46.17, -5.55) * mm});
            skLineSegment(sketch, "E323", {"start": v(46.17, -5.55) * mm, "end": v(46.34, -4.83) * mm});
            skLineSegment(sketch, "E324", {"start": v(46.34, -4.83) * mm, "end": v(46.4, -4.09) * mm});
            skLineSegment(sketch, "E325", {"start": v(46.4, -4.09) * mm, "end": v(46.3, -3.16) * mm});
            skLineSegment(sketch, "E326", {"start": v(46.3, -3.16) * mm, "end": v(46.02, -2.33) * mm});
            skLineSegment(sketch, "E327", {"start": v(46.02, -2.33) * mm, "end": v(45.54, -1.6) * mm});
            skLineSegment(sketch, "E328", {"start": v(45.54, -1.6) * mm, "end": v(45.03, -1.1) * mm});
            skLineSegment(sketch, "E329", {"start": v(45.03, -1.1) * mm, "end": v(44.36, -0.63) * mm});
            skLineSegment(sketch, "E330", {"start": v(44.36, -0.63) * mm, "end": v(43.53, -0.2) * mm});
            skLineSegment(sketch, "E331", {"start": v(43.53, -0.2) * mm, "end": v(42.54, 0.2) * mm});
            skLineSegment(sketch, "E332", {"start": v(42.54, 0.2) * mm, "end": v(42.12, 0.34) * mm});
            skLineSegment(sketch, "E333", {"start": v(42.12, 0.34) * mm, "end": v(41.57, 0.5) * mm});
            skLineSegment(sketch, "E334", {"start": v(41.57, 0.5) * mm, "end": v(40.92, 0.69) * mm});
            skLineSegment(sketch, "E335", {"start": v(40.92, 0.69) * mm, "end": v(40.14, 0.9) * mm});
            skLineSegment(sketch, "E336", {"start": v(40.14, 0.9) * mm, "end": v(39.25, 1.14) * mm});
            skLineSegment(sketch, "E337", {"start": v(39.25, 1.14) * mm, "end": v(38.24, 1.4) * mm});
            skLineSegment(sketch, "E338", {"start": v(38.24, 1.4) * mm, "end": v(37.11, 1.69) * mm});
            skLineSegment(sketch, "E339", {"start": v(37.11, 1.69) * mm, "end": v(35.87, 2) * mm});
            skLineSegment(sketch, "E340", {"start": v(35.87, 2) * mm, "end": v(34.78, 2.28) * mm});
            skLineSegment(sketch, "E341", {"start": v(34.78, 2.28) * mm, "end": v(33.75, 2.58) * mm});
            skLineSegment(sketch, "E342", {"start": v(33.75, 2.58) * mm, "end": v(32.77, 2.88) * mm});
            skLineSegment(sketch, "E343", {"start": v(32.77, 2.88) * mm, "end": v(31.85, 3.2) * mm});
            skLineSegment(sketch, "E344", {"start": v(31.85, 3.2) * mm, "end": v(30.98, 3.52) * mm});
            skLineSegment(sketch, "E345", {"start": v(30.98, 3.52) * mm, "end": v(30.17, 3.85) * mm});
            skLineSegment(sketch, "E346", {"start": v(30.17, 3.85) * mm, "end": v(29.41, 4.2) * mm});
            skLineSegment(sketch, "E347", {"start": v(29.41, 4.2) * mm, "end": v(28.71, 4.56) * mm});
            skLineSegment(sketch, "E348", {"start": v(28.71, 4.56) * mm, "end": v(28.07, 4.92) * mm});
            skLineSegment(sketch, "E349", {"start": v(28.07, 4.92) * mm, "end": v(27.48, 5.3) * mm});
            skLineSegment(sketch, "E350", {"start": v(27.48, 5.3) * mm, "end": v(26.94, 5.69) * mm});
            skLineSegment(sketch, "E351", {"start": v(26.94, 5.69) * mm, "end": v(26.46, 6.09) * mm});
            skLineSegment(sketch, "E352", {"start": v(26.46, 6.09) * mm, "end": v(25.8, 6.72) * mm});
            skLineSegment(sketch, "E353", {"start": v(25.8, 6.72) * mm, "end": v(25.2, 7.38) * mm});
            skLineSegment(sketch, "E354", {"start": v(25.2, 7.38) * mm, "end": v(24.67, 8.06) * mm});
            skLineSegment(sketch, "E355", {"start": v(24.67, 8.06) * mm, "end": v(24.2, 8.76) * mm});
            skLineSegment(sketch, "E356", {"start": v(24.2, 8.76) * mm, "end": v(23.8, 9.5) * mm});
            skLineSegment(sketch, "E357", {"start": v(23.8, 9.5) * mm, "end": v(23.45, 10.25) * mm});
            skLineSegment(sketch, "E358", {"start": v(23.45, 10.25) * mm, "end": v(23.17, 11.03) * mm});
            skLineSegment(sketch, "E359", {"start": v(23.17, 11.03) * mm, "end": v(22.95, 11.83) * mm});
            skLineSegment(sketch, "E360", {"start": v(22.95, 11.83) * mm, "end": v(22.79, 12.66) * mm});
            skLineSegment(sketch, "E361", {"start": v(22.79, 12.66) * mm, "end": v(22.7, 13.52) * mm});
            skLineSegment(sketch, "E362", {"start": v(22.7, 13.52) * mm, "end": v(22.66, 14.4) * mm});
            skLineSegment(sketch, "E363", {"start": v(22.66, 14.4) * mm, "end": v(22.7, 15.3) * mm});
            skLineSegment(sketch, "E364", {"start": v(22.7, 15.3) * mm, "end": v(22.8, 16.17) * mm});
            skLineSegment(sketch, "E365", {"start": v(22.8, 16.17) * mm, "end": v(23, 17.03) * mm});
            skLineSegment(sketch, "E366", {"start": v(23, 17.03) * mm, "end": v(23.25, 17.87) * mm});
            skLineSegment(sketch, "E367", {"start": v(23.25, 17.87) * mm, "end": v(23.58, 18.7) * mm});
            skLineSegment(sketch, "E368", {"start": v(23.58, 18.7) * mm, "end": v(23.98, 19.5) * mm});
            skLineSegment(sketch, "E369", {"start": v(23.98, 19.5) * mm, "end": v(24.45, 20.3) * mm});
            skLineSegment(sketch, "E370", {"start": v(24.45, 20.3) * mm, "end": v(24.92, 20.97) * mm});
            skLineSegment(sketch, "E371", {"start": v(24.92, 20.97) * mm, "end": v(25.44, 21.6) * mm});
            skLineSegment(sketch, "E372", {"start": v(25.44, 21.6) * mm, "end": v(26.01, 22.18) * mm});
            skLineSegment(sketch, "E373", {"start": v(26.01, 22.18) * mm, "end": v(26.63, 22.72) * mm});
            skLineSegment(sketch, "E374", {"start": v(26.63, 22.72) * mm, "end": v(27.3, 23.22) * mm});
            skLineSegment(sketch, "E375", {"start": v(27.3, 23.22) * mm, "end": v(28.02, 23.68) * mm});
            skLineSegment(sketch, "E376", {"start": v(28.02, 23.68) * mm, "end": v(28.79, 24.1) * mm});
            skLineSegment(sketch, "E377", {"start": v(28.79, 24.1) * mm, "end": v(29.6, 24.48) * mm});
            skLineSegment(sketch, "E378", {"start": v(29.6, 24.48) * mm, "end": v(30.37, 24.79) * mm});
            skLineSegment(sketch, "E379", {"start": v(30.37, 24.79) * mm, "end": v(31.16, 25.05) * mm});
            skLineSegment(sketch, "E380", {"start": v(31.16, 25.05) * mm, "end": v(32, 25.28) * mm});
            skLineSegment(sketch, "E381", {"start": v(32, 25.28) * mm, "end": v(32.87, 25.48) * mm});
            skLineSegment(sketch, "E382", {"start": v(32.87, 25.48) * mm, "end": v(33.77, 25.64) * mm});
            skLineSegment(sketch, "E383", {"start": v(33.77, 25.64) * mm, "end": v(34.7, 25.76) * mm});
            skLineSegment(sketch, "E384", {"start": v(34.7, 25.76) * mm, "end": v(35.68, 25.85) * mm});
            skLineSegment(sketch, "E385", {"start": v(35.68, 25.85) * mm, "end": v(36.68, 25.9) * mm});
            skLineSegment(sketch, "E386", {"start": v(36.68, 25.9) * mm, "end": v(37.72, 25.92) * mm});
            skLineSegment(sketch, "E387", {"start": v(37.72, 25.92) * mm, "end": v(38.81, 25.9) * mm});
            skLineSegment(sketch, "E388", {"start": v(38.81, 25.9) * mm, "end": v(39.86, 25.85) * mm});
            skLineSegment(sketch, "E389", {"start": v(39.86, 25.85) * mm, "end": v(40.87, 25.76) * mm});
            skLineSegment(sketch, "E390", {"start": v(40.87, 25.76) * mm, "end": v(41.85, 25.64) * mm});
            skLineSegment(sketch, "E391", {"start": v(41.85, 25.64) * mm, "end": v(42.78, 25.49) * mm});
            skLineSegment(sketch, "E392", {"start": v(42.78, 25.49) * mm, "end": v(43.67, 25.3) * mm});
            skLineSegment(sketch, "E393", {"start": v(43.67, 25.3) * mm, "end": v(44.53, 25.07) * mm});
            skLineSegment(sketch, "E394", {"start": v(44.53, 25.07) * mm, "end": v(45.34, 24.8) * mm});
            skLineSegment(sketch, "E395", {"start": v(45.34, 24.8) * mm, "end": v(46.12, 24.51) * mm});
            skLineSegment(sketch, "E396", {"start": v(46.12, 24.51) * mm, "end": v(46.86, 24.18) * mm});
            skLineSegment(sketch, "E397", {"start": v(46.86, 24.18) * mm, "end": v(47.56, 23.82) * mm});
            skLineSegment(sketch, "E398", {"start": v(47.56, 23.82) * mm, "end": v(48.21, 23.42) * mm});
            skLineSegment(sketch, "E399", {"start": v(48.21, 23.42) * mm, "end": v(48.83, 22.98) * mm});
            skLineSegment(sketch, "E400", {"start": v(48.83, 22.98) * mm, "end": v(49.41, 22.51) * mm});
            skLineSegment(sketch, "E401", {"start": v(49.41, 22.51) * mm, "end": v(50.04, 21.93) * mm});
            skLineSegment(sketch, "E402", {"start": v(50.04, 21.93) * mm, "end": v(50.62, 21.31) * mm});
            skLineSegment(sketch, "E403", {"start": v(50.62, 21.31) * mm, "end": v(51.14, 20.67) * mm});
            skLineSegment(sketch, "E404", {"start": v(51.14, 20.67) * mm, "end": v(51.62, 19.99) * mm});
            skLineSegment(sketch, "E405", {"start": v(51.62, 19.99) * mm, "end": v(52.04, 19.28) * mm});
            skLineSegment(sketch, "E406", {"start": v(52.04, 19.28) * mm, "end": v(52.4, 18.53) * mm});
            skLineSegment(sketch, "E407", {"start": v(52.4, 18.53) * mm, "end": v(52.73, 17.76) * mm});
            skLineSegment(sketch, "E408", {"start": v(52.73, 17.76) * mm, "end": v(53, 16.95) * mm});
            skLineSegment(sketch, "E409", {"start": v(53, 16.95) * mm, "end": v(53.2, 16.12) * mm});
            skLineSegment(sketch, "E410", {"start": v(53.2, 16.12) * mm, "end": v(53.37, 15.25) * mm});
            skLineSegment(sketch, "E411", {"start": v(53.37, 15.25) * mm, "end": v(53.48, 14.35) * mm});
            skLineSegment(sketch, "E412", {"start": v(53.48, 14.35) * mm, "end": v(53.54, 13.41) * mm});
            skLineSegment(sketch, "E413", {"start": v(53.54, 13.41) * mm, "end": v(45.2, 13.04) * mm});
            skLineSegment(sketch, "E414", {"start": v(45.2, 13.04) * mm, "end": v(44.99, 14.06) * mm});
            skLineSegment(sketch, "E415", {"start": v(44.99, 14.06) * mm, "end": v(44.7, 14.97) * mm});
            skLineSegment(sketch, "E416", {"start": v(44.7, 14.97) * mm, "end": v(44.36, 15.78) * mm});
            skLineSegment(sketch, "E417", {"start": v(44.36, 15.78) * mm, "end": v(43.94, 16.5) * mm});
            skLineSegment(sketch, "E418", {"start": v(43.94, 16.5) * mm, "end": v(43.46, 17.11) * mm});
            skLineSegment(sketch, "E419", {"start": v(43.46, 17.11) * mm, "end": v(42.9, 17.63) * mm});
            skLineSegment(sketch, "E420", {"start": v(42.9, 17.63) * mm, "end": v(42.37, 18) * mm});
            skLineSegment(sketch, "E421", {"start": v(42.37, 18) * mm, "end": v(41.76, 18.31) * mm});
            skLineSegment(sketch, "E422", {"start": v(41.76, 18.31) * mm, "end": v(41.08, 18.57) * mm});
            skLineSegment(sketch, "E423", {"start": v(41.08, 18.57) * mm, "end": v(40.32, 18.77) * mm});
            skLineSegment(sketch, "E424", {"start": v(40.32, 18.77) * mm, "end": v(39.5, 18.91) * mm});
            skLineSegment(sketch, "E425", {"start": v(39.5, 18.91) * mm, "end": v(38.6, 19) * mm});
            skLineSegment(sketch, "E426", {"start": v(38.6, 19) * mm, "end": v(37.63, 19.03) * mm});
            skLineSegment(sketch, "E427", {"start": v(37.63, 19.03) * mm, "end": v(36.63, 19) * mm});
            skLineSegment(sketch, "E428", {"start": v(36.63, 19) * mm, "end": v(35.69, 18.9) * mm});
            skLineSegment(sketch, "E429", {"start": v(35.69, 18.9) * mm, "end": v(34.81, 18.75) * mm});
            skLineSegment(sketch, "E430", {"start": v(34.81, 18.75) * mm, "end": v(34, 18.54) * mm});
            skLineSegment(sketch, "E431", {"start": v(34, 18.54) * mm, "end": v(33.25, 18.26) * mm});
            skLineSegment(sketch, "E432", {"start": v(33.25, 18.26) * mm, "end": v(32.57, 17.93) * mm});
            skLineSegment(sketch, "E433", {"start": v(32.57, 17.93) * mm, "end": v(31.95, 17.53) * mm});
            skLineSegment(sketch, "E434", {"start": v(31.95, 17.53) * mm, "end": v(31.37, 17.01) * mm});
            skLineSegment(sketch, "E435", {"start": v(31.37, 17.01) * mm, "end": v(30.96, 16.41) * mm});
            skLineSegment(sketch, "E436", {"start": v(30.96, 16.41) * mm, "end": v(30.71, 15.73) * mm});
            skLineSegment(sketch, "E437", {"start": v(30.71, 15.73) * mm, "end": v(30.63, 14.96) * mm});
            skLineSegment(sketch, "E438", {"start": v(30.63, 14.96) * mm, "end": v(30.7, 14.26) * mm});
            skLineSegment(sketch, "E439", {"start": v(30.7, 14.26) * mm, "end": v(30.94, 13.6) * mm});
            skLineSegment(sketch, "E440", {"start": v(30.94, 13.6) * mm, "end": v(31.33, 13) * mm});
            skLineSegment(sketch, "E441", {"start": v(31.33, 13) * mm, "end": v(31.87, 12.45) * mm});
            skLineSegment(sketch, "E442", {"start": v(31.87, 12.45) * mm, "end": v(32.23, 12.19) * mm});
            skLineSegment(sketch, "E443", {"start": v(32.23, 12.19) * mm, "end": v(32.68, 11.92) * mm});
            skLineSegment(sketch, "E444", {"start": v(32.68, 11.92) * mm, "end": v(33.22, 11.65) * mm});
            skLineSegment(sketch, "E445", {"start": v(33.22, 11.65) * mm, "end": v(33.85, 11.37) * mm});
            skLineSegment(sketch, "E446", {"start": v(33.85, 11.37) * mm, "end": v(34.57, 11.1) * mm});
            skLineSegment(sketch, "E447", {"start": v(34.57, 11.1) * mm, "end": v(35.38, 10.82) * mm});
            skLineSegment(sketch, "E448", {"start": v(35.38, 10.82) * mm, "end": v(36.28, 10.54) * mm});
            skLineSegment(sketch, "E449", {"start": v(36.28, 10.54) * mm, "end": v(37.28, 10.26) * mm});
            skLineSegment(sketch, "E450", {"start": v(37.28, 10.26) * mm, "end": v(38.36, 9.98) * mm});
            skLineSegment(sketch, "E451", {"start": v(38.36, 9.98) * mm, "end": v(39.53, 9.7) * mm});
            skLineSegment(sketch, "E452", {"start": v(39.53, 9.7) * mm, "end": v(40.6, 9.43) * mm});
            skLineSegment(sketch, "E453", {"start": v(40.6, 9.43) * mm, "end": v(41.64, 9.17) * mm});
            skLineSegment(sketch, "E454", {"start": v(41.64, 9.17) * mm, "end": v(42.61, 8.9) * mm});
            skLineSegment(sketch, "E455", {"start": v(42.61, 8.9) * mm, "end": v(43.53, 8.63) * mm});
            skLineSegment(sketch, "E456", {"start": v(43.53, 8.63) * mm, "end": v(44.4, 8.36) * mm});
            skLineSegment(sketch, "E457", {"start": v(44.4, 8.36) * mm, "end": v(45.22, 8.1) * mm});
            skLineSegment(sketch, "E458", {"start": v(45.22, 8.1) * mm, "end": v(45.99, 7.82) * mm});
            skLineSegment(sketch, "E459", {"start": v(45.99, 7.82) * mm, "end": v(46.7, 7.55) * mm});
            skLineSegment(sketch, "E460", {"start": v(46.7, 7.55) * mm, "end": v(47.36, 7.27) * mm});
            skLineSegment(sketch, "E461", {"start": v(47.36, 7.27) * mm, "end": v(47.97, 7) * mm});
            skLineSegment(sketch, "E462", {"start": v(47.97, 7) * mm, "end": v(48.53, 6.72) * mm});
            skLineSegment(sketch, "E463", {"start": v(48.53, 6.72) * mm, "end": v(49.33, 6.26) * mm});
            skLineSegment(sketch, "E464", {"start": v(49.33, 6.26) * mm, "end": v(50.09, 5.75) * mm});
            skLineSegment(sketch, "E465", {"start": v(50.09, 5.75) * mm, "end": v(50.8, 5.2) * mm});
            skLineSegment(sketch, "E466", {"start": v(50.8, 5.2) * mm, "end": v(51.44, 4.6) * mm});
            skLineSegment(sketch, "E467", {"start": v(51.44, 4.6) * mm, "end": v(52.04, 3.95) * mm});
            skLineSegment(sketch, "E468", {"start": v(52.04, 3.95) * mm, "end": v(52.6, 3.26) * mm});
            skLineSegment(sketch, "E469", {"start": v(52.6, 3.26) * mm, "end": v(53.09, 2.53) * mm});
            skLineSegment(sketch, "E470", {"start": v(53.09, 2.53) * mm, "end": v(53.47, 1.84) * mm});
            skLineSegment(sketch, "E471", {"start": v(53.47, 1.84) * mm, "end": v(53.8, 1.12) * mm});
            skLineSegment(sketch, "E472", {"start": v(53.8, 1.12) * mm, "end": v(54.1, 0.35) * mm});
            skLineSegment(sketch, "E473", {"start": v(54.1, 0.35) * mm, "end": v(54.32, -0.45) * mm});
            skLineSegment(sketch, "E474", {"start": v(54.32, -0.45) * mm, "end": v(54.5, -1.29) * mm});
            skLineSegment(sketch, "E475", {"start": v(54.5, -1.29) * mm, "end": v(54.63, -2.17) * mm});
            skLineSegment(sketch, "E476", {"start": v(54.63, -2.17) * mm, "end": v(54.7, -3.09) * mm});
            skLineSegment(sketch, "E477", {"start": v(54.7, -3.09) * mm, "end": v(54.73, -4.05) * mm});
            skLineSegment(sketch, "E478", {"start": v(54.73, -4.05) * mm, "end": v(54.7, -4.93) * mm});
            skLineSegment(sketch, "E479", {"start": v(54.7, -4.93) * mm, "end": v(54.61, -5.8) * mm});
            skLineSegment(sketch, "E480", {"start": v(54.61, -5.8) * mm, "end": v(54.46, -6.64) * mm});
            skLineSegment(sketch, "E481", {"start": v(54.46, -6.64) * mm, "end": v(54.24, -7.48) * mm});
            skLineSegment(sketch, "E482", {"start": v(54.24, -7.48) * mm, "end": v(53.96, -8.3) * mm});
            skLineSegment(sketch, "E483", {"start": v(53.96, -8.3) * mm, "end": v(53.63, -9.11) * mm});
            skLineSegment(sketch, "E484", {"start": v(53.63, -9.11) * mm, "end": v(53.23, -9.9) * mm});
            skLineSegment(sketch, "E485", {"start": v(53.23, -9.9) * mm, "end": v(52.76, -10.7) * mm});
            skLineSegment(sketch, "E486", {"start": v(52.76, -10.7) * mm, "end": v(52.25, -11.44) * mm});
            skLineSegment(sketch, "E487", {"start": v(52.25, -11.44) * mm, "end": v(51.68, -12.14) * mm});
            skLineSegment(sketch, "E488", {"start": v(51.68, -12.14) * mm, "end": v(51.06, -12.79) * mm});
            skLineSegment(sketch, "E489", {"start": v(51.06, -12.79) * mm, "end": v(50.39, -13.39) * mm});
            skLineSegment(sketch, "E490", {"start": v(50.39, -13.39) * mm, "end": v(49.66, -13.94) * mm});
            skLineSegment(sketch, "E491", {"start": v(49.66, -13.94) * mm, "end": v(48.89, -14.44) * mm});
            skLineSegment(sketch, "E492", {"start": v(48.89, -14.44) * mm, "end": v(48.07, -14.9) * mm});
            skLineSegment(sketch, "E493", {"start": v(48.07, -14.9) * mm, "end": v(47.2, -15.3) * mm});
            skLineSegment(sketch, "E494", {"start": v(47.2, -15.3) * mm, "end": v(46.45, -15.58) * mm});
            skLineSegment(sketch, "E495", {"start": v(46.45, -15.58) * mm, "end": v(45.68, -15.84) * mm});
            skLineSegment(sketch, "E496", {"start": v(45.68, -15.84) * mm, "end": v(44.87, -16.06) * mm});
            skLineSegment(sketch, "E497", {"start": v(44.87, -16.06) * mm, "end": v(44.02, -16.26) * mm});
            skLineSegment(sketch, "E498", {"start": v(44.02, -16.26) * mm, "end": v(43.14, -16.42) * mm});
            skLineSegment(sketch, "E499", {"start": v(43.14, -16.42) * mm, "end": v(42.23, -16.56) * mm});
            skLineSegment(sketch, "E500", {"start": v(42.23, -16.56) * mm, "end": v(41.28, -16.66) * mm});
            skLineSegment(sketch, "E501", {"start": v(41.28, -16.66) * mm, "end": v(40.29, -16.74) * mm});
            skLineSegment(sketch, "E502", {"start": v(40.29, -16.74) * mm, "end": v(39.27, -16.78) * mm});
            skLineSegment(sketch, "E503", {"start": v(39.27, -16.78) * mm, "end": v(38.2, -16.8) * mm});
            skLineSegment(sketch, "E504", {"start": v(38.2, -16.8) * mm, "end": v(37.11, -16.78) * mm});
            skLineSegment(sketch, "E505", {"start": v(37.11, -16.78) * mm, "end": v(36.05, -16.73) * mm});
            skLineSegment(sketch, "E506", {"start": v(36.05, -16.73) * mm, "end": v(35.02, -16.63) * mm});
            skLineSegment(sketch, "E507", {"start": v(35.02, -16.63) * mm, "end": v(34.03, -16.5) * mm});
            skLineSegment(sketch, "E508", {"start": v(34.03, -16.5) * mm, "end": v(33.08, -16.34) * mm});
            skLineSegment(sketch, "E509", {"start": v(33.08, -16.34) * mm, "end": v(32.17, -16.13) * mm});
            skLineSegment(sketch, "E510", {"start": v(32.17, -16.13) * mm, "end": v(31.3, -15.9) * mm});
            skLineSegment(sketch, "E511", {"start": v(31.3, -15.9) * mm, "end": v(30.45, -15.62) * mm});
            skLineSegment(sketch, "E512", {"start": v(30.45, -15.62) * mm, "end": v(29.65, -15.3) * mm});
            skLineSegment(sketch, "E513", {"start": v(29.65, -15.3) * mm, "end": v(28.88, -14.95) * mm});
            skLineSegment(sketch, "E514", {"start": v(28.88, -14.95) * mm, "end": v(28.15, -14.57) * mm});
            skLineSegment(sketch, "E515", {"start": v(28.15, -14.57) * mm, "end": v(27.46, -14.14) * mm});
            skLineSegment(sketch, "E516", {"start": v(27.46, -14.14) * mm, "end": v(26.8, -13.68) * mm});
            skLineSegment(sketch, "E517", {"start": v(26.8, -13.68) * mm, "end": v(26.19, -13.18) * mm});
            skLineSegment(sketch, "E518", {"start": v(26.19, -13.18) * mm, "end": v(25.56, -12.6) * mm});
            skLineSegment(sketch, "E519", {"start": v(25.56, -12.6) * mm, "end": v(24.98, -12) * mm});
            skLineSegment(sketch, "E520", {"start": v(24.98, -12) * mm, "end": v(24.43, -11.34) * mm});
            skLineSegment(sketch, "E521", {"start": v(24.43, -11.34) * mm, "end": v(23.93, -10.64) * mm});
            skLineSegment(sketch, "E522", {"start": v(23.93, -10.64) * mm, "end": v(23.46, -9.91) * mm});
            skLineSegment(sketch, "E523", {"start": v(23.46, -9.91) * mm, "end": v(23.04, -9.14) * mm});
            skLineSegment(sketch, "E524", {"start": v(23.04, -9.14) * mm, "end": v(22.65, -8.33) * mm});
            skLineSegment(sketch, "E525", {"start": v(22.65, -8.33) * mm, "end": v(22.3, -7.48) * mm});
            skLineSegment(sketch, "E526", {"start": v(22.3, -7.48) * mm, "end": v(22, -6.59) * mm});
            skLineSegment(sketch, "E527", {"start": v(22, -6.59) * mm, "end": v(21.73, -5.66) * mm});
            skLineSegment(sketch, "E528", {"start": v(21.73, -5.66) * mm, "end": v(21.5, -4.7) * mm});
            skLineSegment(sketch, "E529", {"start": v(21.5, -4.7) * mm, "end": v(21.32, -3.69) * mm});
            skLineSegment(sketch, "E530", {"start": v(21.32, -3.69) * mm, "end": v(21.18, -2.64) * mm});
            skLineSegment(sketch, "E531", {"start": v(65.89, -16.01) * mm, "end": v(65.89, 25.26) * mm});
            skLineSegment(sketch, "E532", {"start": v(65.89, 25.26) * mm, "end": v(96.43, 25.26) * mm});
            skLineSegment(sketch, "E533", {"start": v(96.43, 25.26) * mm, "end": v(96.43, 18.28) * mm});
            skLineSegment(sketch, "E534", {"start": v(96.43, 18.28) * mm, "end": v(74.23, 18.28) * mm});
            skLineSegment(sketch, "E535", {"start": v(74.23, 18.28) * mm, "end": v(74.23, 9.12) * mm});
            skLineSegment(sketch, "E536", {"start": v(74.23, 9.12) * mm, "end": v(94.9, 9.12) * mm});
            skLineSegment(sketch, "E537", {"start": v(94.9, 9.12) * mm, "end": v(94.9, 2.15) * mm});
            skLineSegment(sketch, "E538", {"start": v(94.9, 2.15) * mm, "end": v(74.23, 2.15) * mm});
            skLineSegment(sketch, "E539", {"start": v(74.23, 2.15) * mm, "end": v(74.23, -9.04) * mm});
            skLineSegment(sketch, "E540", {"start": v(74.23, -9.04) * mm, "end": v(97.22, -9.04) * mm});
            skLineSegment(sketch, "E541", {"start": v(97.22, -9.04) * mm, "end": v(97.22, -16.01) * mm});
            skLineSegment(sketch, "E542", {"start": v(97.22, -16.01) * mm, "end": v(65.89, -16.01) * mm});
            skLineSegment(sketch, "E543", {"start": v(108.53, -16.01) * mm, "end": v(108.53, 25.26) * mm});
            skLineSegment(sketch, "E544", {"start": v(108.53, 25.26) * mm, "end": v(116.62, 25.26) * mm});
            skLineSegment(sketch, "E545", {"start": v(116.62, 25.26) * mm, "end": v(133.5, -2.35) * mm});
            skLineSegment(sketch, "E546", {"start": v(133.5, -2.35) * mm, "end": v(133.5, 25.26) * mm});
            skLineSegment(sketch, "E547", {"start": v(133.5, 25.26) * mm, "end": v(141.22, 25.26) * mm});
            skLineSegment(sketch, "E548", {"start": v(141.22, 25.26) * mm, "end": v(141.22, -16.01) * mm});
            skLineSegment(sketch, "E549", {"start": v(141.22, -16.01) * mm, "end": v(132.89, -16.01) * mm});
            skLineSegment(sketch, "E550", {"start": v(132.89, -16.01) * mm, "end": v(116.25, 11.02) * mm});
            skLineSegment(sketch, "E551", {"start": v(116.25, 11.02) * mm, "end": v(116.25, -16.01) * mm});
            skLineSegment(sketch, "E552", {"start": v(116.25, -16.01) * mm, "end": v(108.53, -16.01) * mm});
            skSolve(sketch);
        }
        {
            var Q0;
            Q0=makeQuery(id+"F0.imprint","IMPRINT",FACE,{"disambiguationData":[TD([[makeQuery(id+"F0.imprint","IMPRINT",EDGE,{"derivedFrom":sQuery(id+"F0.wireOp",EDGE,"E0")}),1.0]])]});
            extrude(context, id + "F1", {"entities" : qUnion([Q0]), "depth" : 25.4 * mm, "offsetDistance" : 25.4 * mm});
        }
    });
